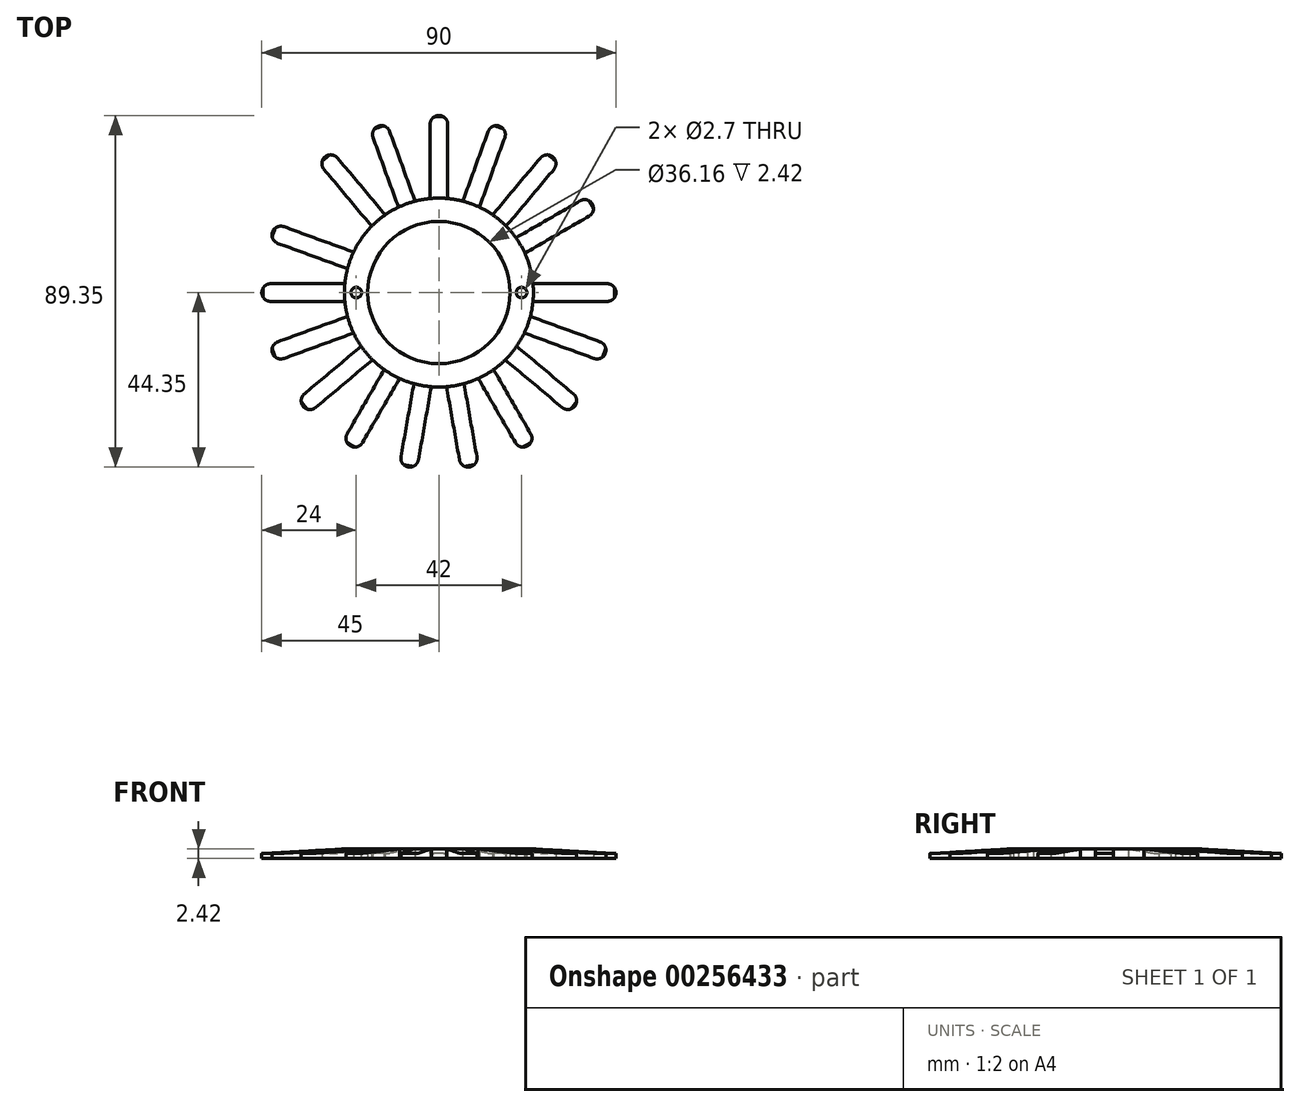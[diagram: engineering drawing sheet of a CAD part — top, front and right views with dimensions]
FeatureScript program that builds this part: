
annotation { "Feature Type Name" : "Feature", "Feature Type Description" : "" }
export const myFeature = defineFeature(function(context is Context, id is Id, definition is map)
    precondition{}
    {
        {
            var Q0;
            Q0=qCreatedBy(makeId("Top.planeOp"),FACE);
            var sketch = newSketch(context, id + "F0", { "sketchPlane" : qUnion([Q0])});
            skCircle(sketch, "E0", {"center": v(0, 0) * mm, "radius": 6.03 * mm});
            skCircle(sketch, "E1", {"center": v(0, 0) * mm, "radius": 8 * mm});
            skSolve(sketch);
        }
        {
            var Q0;
            Q0=makeQuery(id+"F0.imprint","IMPRINT",FACE,{"disambiguationData":[TD([[makeQuery(id+"F0.imprint","IMPRINT",EDGE,{"derivedFrom":sQuery(id+"F0.wireOp",EDGE,"E0")}),-1.0]])]});
            extrude(context, id + "F1", {"entities" : qUnion([Q0]), "depth" : 0.34 * mm});
        }
        {
            var Q0;
            Q0=qCreatedBy(makeId("Top.planeOp"),FACE);
            var sketch = newSketch(context, id + "F2", { "sketchPlane" : qUnion([Q0])});
            skCircle(sketch, "E2", {"center": v(0, 0) * mm, "radius": 8 * mm, "construction": true});
            skCircle(sketch, "E3", {"center": v(0, 0) * mm, "radius": 15 * mm, "construction": true});
            skArc(sketch, "E4", {"start": v(14.25, -0.75) * mm, "mid": v(15, 0) * mm, "end": v(14.25, 0.75) * mm});
            skLineSegment(sketch, "E5", {"start": v(14.25, -0.75) * mm, "end": v(7.96, -0.75) * mm});
            skLineSegment(sketch, "E6", {"start": v(14.25, 0.75) * mm, "end": v(7.96, 0.75) * mm});
            skLineSegment(sketch, "E7", {"start": v(7.96, 0.75) * mm, "end": v(7.96, -0.75) * mm});
            skSolve(sketch);
        }
        {
            var Q0;
            Q0=makeQuery(id+"F2.imprint","IMPRINT",FACE,{"disambiguationData":[TD([[makeQuery(id+"F2.imprint","IMPRINT",EDGE,{"derivedFrom":sQuery(id+"F2.wireOp",EDGE,"E4")}),1.0]])]});
            extrude(context, id + "F3", {"entities" : qUnion([Q0]), "depth" : 0.34 * mm});
        }
        {
            var Q0;
            Q0=qCreatedBy(makeId("Front.planeOp"),FACE);
            var sketch = newSketch(context, id + "F4", { "sketchPlane" : qUnion([Q0])});
            skLineSegment(sketch, "E8", {"start": v(0, 0) * mm, "end": v(0, 5.33) * mm, "construction": true});
            skSolve(sketch);
        }
        {
            var Q0;
            Q0=makeQuery(id+"F3.opExtrude","SWEPT_BODY",BODY,{"disambiguationData":[OSD([sQuery(id+"F2.wireOp",EDGE,"E4"),sQuery(id+"F2.wireOp",EDGE,"E5"),sQuery(id+"F2.wireOp",EDGE,"E6"),sQuery(id+"F2.wireOp",EDGE,"E7")])]});
            var Q1;
            Q1=sQuery(id+"F4.wireOp",EDGE,"E8");
            circularPattern(context, id + "F5", {"entities" : qUnion([Q0]), "axis" : qUnion([Q1]), "angle" : 20 * degree, "instanceCount" : 11, "oppositeDirection" : true, "computeTransformsWithoutBuiltin" : true});
        }
        {
            var Q0;
            Q0=qCreatedBy(makeId("Top.planeOp"),FACE);
            var sketch = newSketch(context, id + "F6", { "sketchPlane" : qUnion([Q0])});
            skCircle(sketch, "E9", {"center": v(0, 0) * mm, "radius": 15 * mm, "construction": true});
            skLineSegment(sketch, "E10", {"start": v(0, 0) * mm, "end": v(13, 7.5) * mm, "construction": true});
            skLineSegment(sketch, "E11", {"start": v(0, 0) * mm, "end": v(13.86, 0) * mm, "construction": true});
            skArc(sketch, "E12", {"start": v(12.72, 6.48) * mm, "mid": v(13, 7.5) * mm, "end": v(11.97, 7.77) * mm});
            skLineSegment(sketch, "E13", {"start": v(12.34, 7.13) * mm, "end": v(12.72, 6.48) * mm});
            skLineSegment(sketch, "E14", {"start": v(12.72, 6.48) * mm, "end": v(6.65, 2.98) * mm});
            skLineSegment(sketch, "E15", {"start": v(6.65, 2.98) * mm, "end": v(5.9, 4.27) * mm});
            skLineSegment(sketch, "E16", {"start": v(5.9, 4.27) * mm, "end": v(11.97, 7.77) * mm});
            skSolve(sketch);
        }
        {
            var Q0;
            Q0=makeQuery(id+"F6.imprint","IMPRINT",FACE,{"disambiguationData":[TD([[makeQuery(id+"F6.imprint","IMPRINT",EDGE,{"derivedFrom":sQuery(id+"F6.wireOp",EDGE,"E12")}),1.0]])]});
            extrude(context, id + "F7", {"entities" : qUnion([Q0]), "depth" : 0.34 * mm});
        }
        {
            var Q0;
            Q0=makeQuery(id+"F7.opExtrude","SWEPT_BODY",BODY,{"disambiguationData":[OSD([sQuery(id+"F6.wireOp",EDGE,"E12"),sQuery(id+"F6.wireOp",EDGE,"E14"),sQuery(id+"F6.wireOp",EDGE,"E15"),sQuery(id+"F6.wireOp",EDGE,"E16")])]});
            var Q1;
            Q1=sQuery(id+"F4.wireOp",EDGE,"E8");
            circularPattern(context, id + "F8", {"entities" : qUnion([Q0]), "axis" : qUnion([Q1]), "angle" : 20 * degree, "instanceCount" : 6, "computeTransformsWithoutBuiltin" : true});
        }
        {
            var Q0;
            Q0=makeQuery(id+"F1.opExtrude","SWEPT_BODY",BODY,{"disambiguationData":[OSD([sQuery(id+"F0.wireOp",EDGE,"E0"),sQuery(id+"F0.wireOp",EDGE,"E1")])]});
            var Q1;
            Q1=makeQuery(id+"F7.opExtrude","SWEPT_BODY",BODY,{"disambiguationData":[OSD([sQuery(id+"F6.wireOp",EDGE,"E12"),sQuery(id+"F6.wireOp",EDGE,"E14"),sQuery(id+"F6.wireOp",EDGE,"E15"),sQuery(id+"F6.wireOp",EDGE,"E16")])]});
            var Q2;
            Q2=makeQuery(id+"F8.opPattern","COPY",BODY,{"derivedFrom":makeQuery(id+"F7.opExtrude","SWEPT_BODY",BODY,{"disambiguationData":[OSD([sQuery(id+"F6.wireOp",EDGE,"E12"),sQuery(id+"F6.wireOp",EDGE,"E14"),sQuery(id+"F6.wireOp",EDGE,"E15"),sQuery(id+"F6.wireOp",EDGE,"E16")])]}),"instanceName":"1"});
            var Q3;
            Q3=makeQuery(id+"F8.opPattern","COPY",BODY,{"derivedFrom":makeQuery(id+"F7.opExtrude","SWEPT_BODY",BODY,{"disambiguationData":[OSD([sQuery(id+"F6.wireOp",EDGE,"E12"),sQuery(id+"F6.wireOp",EDGE,"E14"),sQuery(id+"F6.wireOp",EDGE,"E15"),sQuery(id+"F6.wireOp",EDGE,"E16")])]}),"instanceName":"2"});
            var Q4;
            Q4=makeQuery(id+"F8.opPattern","COPY",BODY,{"derivedFrom":makeQuery(id+"F7.opExtrude","SWEPT_BODY",BODY,{"disambiguationData":[OSD([sQuery(id+"F6.wireOp",EDGE,"E12"),sQuery(id+"F6.wireOp",EDGE,"E14"),sQuery(id+"F6.wireOp",EDGE,"E15"),sQuery(id+"F6.wireOp",EDGE,"E16")])]}),"instanceName":"3"});
            var Q5;
            Q5=makeQuery(id+"F8.opPattern","COPY",BODY,{"derivedFrom":makeQuery(id+"F7.opExtrude","SWEPT_BODY",BODY,{"disambiguationData":[OSD([sQuery(id+"F6.wireOp",EDGE,"E12"),sQuery(id+"F6.wireOp",EDGE,"E14"),sQuery(id+"F6.wireOp",EDGE,"E15"),sQuery(id+"F6.wireOp",EDGE,"E16")])]}),"instanceName":"4"});
            var Q6;
            Q6=makeQuery(id+"F8.opPattern","COPY",BODY,{"derivedFrom":makeQuery(id+"F7.opExtrude","SWEPT_BODY",BODY,{"disambiguationData":[OSD([sQuery(id+"F6.wireOp",EDGE,"E12"),sQuery(id+"F6.wireOp",EDGE,"E14"),sQuery(id+"F6.wireOp",EDGE,"E15"),sQuery(id+"F6.wireOp",EDGE,"E16")])]}),"instanceName":"5"});
            var Q7;
            Q7=makeQuery(id+"F5.opPattern","COPY",BODY,{"derivedFrom":makeQuery(id+"F3.opExtrude","SWEPT_BODY",BODY,{"disambiguationData":[OSD([sQuery(id+"F2.wireOp",EDGE,"E4"),sQuery(id+"F2.wireOp",EDGE,"E5"),sQuery(id+"F2.wireOp",EDGE,"E6"),sQuery(id+"F2.wireOp",EDGE,"E7")])]}),"instanceName":"10"});
            var Q8;
            Q8=makeQuery(id+"F5.opPattern","COPY",BODY,{"derivedFrom":makeQuery(id+"F3.opExtrude","SWEPT_BODY",BODY,{"disambiguationData":[OSD([sQuery(id+"F2.wireOp",EDGE,"E4"),sQuery(id+"F2.wireOp",EDGE,"E5"),sQuery(id+"F2.wireOp",EDGE,"E6"),sQuery(id+"F2.wireOp",EDGE,"E7")])]}),"instanceName":"9"});
            var Q9;
            Q9=makeQuery(id+"F5.opPattern","COPY",BODY,{"derivedFrom":makeQuery(id+"F3.opExtrude","SWEPT_BODY",BODY,{"disambiguationData":[OSD([sQuery(id+"F2.wireOp",EDGE,"E4"),sQuery(id+"F2.wireOp",EDGE,"E5"),sQuery(id+"F2.wireOp",EDGE,"E6"),sQuery(id+"F2.wireOp",EDGE,"E7")])]}),"instanceName":"8"});
            var Q10;
            Q10=makeQuery(id+"F5.opPattern","COPY",BODY,{"derivedFrom":makeQuery(id+"F3.opExtrude","SWEPT_BODY",BODY,{"disambiguationData":[OSD([sQuery(id+"F2.wireOp",EDGE,"E4"),sQuery(id+"F2.wireOp",EDGE,"E5"),sQuery(id+"F2.wireOp",EDGE,"E6"),sQuery(id+"F2.wireOp",EDGE,"E7")])]}),"instanceName":"7"});
            var Q11;
            Q11=makeQuery(id+"F5.opPattern","COPY",BODY,{"derivedFrom":makeQuery(id+"F3.opExtrude","SWEPT_BODY",BODY,{"disambiguationData":[OSD([sQuery(id+"F2.wireOp",EDGE,"E4"),sQuery(id+"F2.wireOp",EDGE,"E5"),sQuery(id+"F2.wireOp",EDGE,"E6"),sQuery(id+"F2.wireOp",EDGE,"E7")])]}),"instanceName":"6"});
            var Q12;
            Q12=makeQuery(id+"F5.opPattern","COPY",BODY,{"derivedFrom":makeQuery(id+"F3.opExtrude","SWEPT_BODY",BODY,{"disambiguationData":[OSD([sQuery(id+"F2.wireOp",EDGE,"E4"),sQuery(id+"F2.wireOp",EDGE,"E5"),sQuery(id+"F2.wireOp",EDGE,"E6"),sQuery(id+"F2.wireOp",EDGE,"E7")])]}),"instanceName":"4"});
            var Q13;
            Q13=makeQuery(id+"F5.opPattern","COPY",BODY,{"derivedFrom":makeQuery(id+"F3.opExtrude","SWEPT_BODY",BODY,{"disambiguationData":[OSD([sQuery(id+"F2.wireOp",EDGE,"E4"),sQuery(id+"F2.wireOp",EDGE,"E5"),sQuery(id+"F2.wireOp",EDGE,"E6"),sQuery(id+"F2.wireOp",EDGE,"E7")])]}),"instanceName":"5"});
            var Q14;
            Q14=makeQuery(id+"F5.opPattern","COPY",BODY,{"derivedFrom":makeQuery(id+"F3.opExtrude","SWEPT_BODY",BODY,{"disambiguationData":[OSD([sQuery(id+"F2.wireOp",EDGE,"E4"),sQuery(id+"F2.wireOp",EDGE,"E5"),sQuery(id+"F2.wireOp",EDGE,"E6"),sQuery(id+"F2.wireOp",EDGE,"E7")])]}),"instanceName":"3"});
            var Q15;
            Q15=makeQuery(id+"F5.opPattern","COPY",BODY,{"derivedFrom":makeQuery(id+"F3.opExtrude","SWEPT_BODY",BODY,{"disambiguationData":[OSD([sQuery(id+"F2.wireOp",EDGE,"E4"),sQuery(id+"F2.wireOp",EDGE,"E5"),sQuery(id+"F2.wireOp",EDGE,"E6"),sQuery(id+"F2.wireOp",EDGE,"E7")])]}),"instanceName":"2"});
            var Q16;
            Q16=makeQuery(id+"F5.opPattern","COPY",BODY,{"derivedFrom":makeQuery(id+"F3.opExtrude","SWEPT_BODY",BODY,{"disambiguationData":[OSD([sQuery(id+"F2.wireOp",EDGE,"E4"),sQuery(id+"F2.wireOp",EDGE,"E5"),sQuery(id+"F2.wireOp",EDGE,"E6"),sQuery(id+"F2.wireOp",EDGE,"E7")])]}),"instanceName":"1"});
            var Q17;
            Q17=makeQuery(id+"F3.opExtrude","SWEPT_BODY",BODY,{"disambiguationData":[OSD([sQuery(id+"F2.wireOp",EDGE,"E4"),sQuery(id+"F2.wireOp",EDGE,"E5"),sQuery(id+"F2.wireOp",EDGE,"E6"),sQuery(id+"F2.wireOp",EDGE,"E7")])]});
            booleanBodies(context, id + "F9", {"operationType" : BooleanOperationType.UNION, "tools" : qUnion([Q0, Q1, Q2, Q3, Q4, Q5, Q6, Q7, Q8, Q9, Q10, Q11, Q12, Q13, Q14, Q15, Q16, Q17])});
        }
        {
            var Q0;
            {var subQ0=makeQuery(id+"F3.opExtrude","CAP_FACE",FACE,{"disambiguationData":[OSD([sQuery(id+"F2.wireOp",EDGE,"E4"),sQuery(id+"F2.wireOp",EDGE,"E5"),sQuery(id+"F2.wireOp",EDGE,"E6"),sQuery(id+"F2.wireOp",EDGE,"E7")])],"isStart":false});var subQ1=makeQuery(id+"F7.opExtrude","CAP_FACE",FACE,{"disambiguationData":[OSD([sQuery(id+"F6.wireOp",EDGE,"E12"),sQuery(id+"F6.wireOp",EDGE,"E14"),sQuery(id+"F6.wireOp",EDGE,"E15"),sQuery(id+"F6.wireOp",EDGE,"E16")])],"isStart":false});Q0=makeQuery(id+"F9.opBoolean","MERGE",FACE,{"derivedFrom":[makeQuery(id+"F1.opExtrude","CAP_FACE",FACE,{"disambiguationData":[OSD([sQuery(id+"F0.wireOp",EDGE,"E0"),sQuery(id+"F0.wireOp",EDGE,"E1")])],"isStart":false}),subQ0,makeQuery(id+"F5.opPattern","COPY",FACE,{"derivedFrom":subQ0,"instanceName":"1"}),makeQuery(id+"F5.opPattern","COPY",FACE,{"derivedFrom":subQ0,"instanceName":"2"}),makeQuery(id+"F5.opPattern","COPY",FACE,{"derivedFrom":subQ0,"instanceName":"3"}),makeQuery(id+"F5.opPattern","COPY",FACE,{"derivedFrom":subQ0,"instanceName":"4"}),makeQuery(id+"F5.opPattern","COPY",FACE,{"derivedFrom":subQ0,"instanceName":"5"}),makeQuery(id+"F5.opPattern","COPY",FACE,{"derivedFrom":subQ0,"instanceName":"6"}),makeQuery(id+"F5.opPattern","COPY",FACE,{"derivedFrom":subQ0,"instanceName":"7"}),makeQuery(id+"F5.opPattern","COPY",FACE,{"derivedFrom":subQ0,"instanceName":"8"}),makeQuery(id+"F5.opPattern","COPY",FACE,{"derivedFrom":subQ0,"instanceName":"9"}),makeQuery(id+"F5.opPattern","COPY",FACE,{"derivedFrom":subQ0,"instanceName":"10"}),subQ1,makeQuery(id+"F8.opPattern","COPY",FACE,{"derivedFrom":subQ1,"instanceName":"1"}),makeQuery(id+"F8.opPattern","COPY",FACE,{"derivedFrom":subQ1,"instanceName":"2"}),makeQuery(id+"F8.opPattern","COPY",FACE,{"derivedFrom":subQ1,"instanceName":"3"}),makeQuery(id+"F8.opPattern","COPY",FACE,{"derivedFrom":subQ1,"instanceName":"4"}),makeQuery(id+"F8.opPattern","COPY",FACE,{"derivedFrom":subQ1,"instanceName":"5"})]});}
            var sketch = newSketch(context, id + "F10", { "sketchPlane" : qUnion([Q0])});
            skCircle(sketch, "E17", {"center": v(0, 0) * mm, "radius": 7 * mm, "construction": true});
            skCircle(sketch, "E18", {"center": v(7, 0) * mm, "radius": 0.45 * mm});
            skCircle(sketch, "E19", {"center": v(-7, 0) * mm, "radius": 0.45 * mm});
            skSolve(sketch);
        }
        {
            var Q0;
            {Q0=qUnion([makeQuery(id+"F10.imprint","IMPRINT",FACE,{"disambiguationData":[TD([[makeQuery(id+"F10.imprint","IMPRINT",EDGE,{"derivedFrom":sQuery(id+"F10.wireOp",EDGE,"E18")}),1.0]])]}),makeQuery(id+"F10.imprint","IMPRINT",FACE,{"disambiguationData":[TD([[makeQuery(id+"F10.imprint","IMPRINT",EDGE,{"derivedFrom":sQuery(id+"F10.wireOp",EDGE,"E19")}),1.0]])]})]);}
            var Q2;
            {var subQ0=makeQuery(id+"F7.opExtrude","CAP_FACE",FACE,{"disambiguationData":[OSD([sQuery(id+"F6.wireOp",EDGE,"E12"),sQuery(id+"F6.wireOp",EDGE,"E14"),sQuery(id+"F6.wireOp",EDGE,"E15"),sQuery(id+"F6.wireOp",EDGE,"E16")])],"isStart":true});var subQ1=makeQuery(id+"F3.opExtrude","CAP_FACE",FACE,{"disambiguationData":[OSD([sQuery(id+"F2.wireOp",EDGE,"E4"),sQuery(id+"F2.wireOp",EDGE,"E5"),sQuery(id+"F2.wireOp",EDGE,"E6"),sQuery(id+"F2.wireOp",EDGE,"E7")])],"isStart":true});Q2=makeQuery(id+"F9.opBoolean","MERGE",FACE,{"derivedFrom":[makeQuery(id+"F1.opExtrude","CAP_FACE",FACE,{"disambiguationData":[OSD([sQuery(id+"F0.wireOp",EDGE,"E0"),sQuery(id+"F0.wireOp",EDGE,"E1")])],"isStart":true}),subQ1,makeQuery(id+"F5.opPattern","COPY",FACE,{"derivedFrom":subQ1,"instanceName":"1"}),makeQuery(id+"F5.opPattern","COPY",FACE,{"derivedFrom":subQ1,"instanceName":"2"}),makeQuery(id+"F5.opPattern","COPY",FACE,{"derivedFrom":subQ1,"instanceName":"3"}),makeQuery(id+"F5.opPattern","COPY",FACE,{"derivedFrom":subQ1,"instanceName":"4"}),makeQuery(id+"F5.opPattern","COPY",FACE,{"derivedFrom":subQ1,"instanceName":"5"}),makeQuery(id+"F5.opPattern","COPY",FACE,{"derivedFrom":subQ1,"instanceName":"6"}),makeQuery(id+"F5.opPattern","COPY",FACE,{"derivedFrom":subQ1,"instanceName":"7"}),makeQuery(id+"F5.opPattern","COPY",FACE,{"derivedFrom":subQ1,"instanceName":"8"}),makeQuery(id+"F5.opPattern","COPY",FACE,{"derivedFrom":subQ1,"instanceName":"9"}),makeQuery(id+"F5.opPattern","COPY",FACE,{"derivedFrom":subQ1,"instanceName":"10"}),subQ0,makeQuery(id+"F8.opPattern","COPY",FACE,{"derivedFrom":subQ0,"instanceName":"1"}),makeQuery(id+"F8.opPattern","COPY",FACE,{"derivedFrom":subQ0,"instanceName":"2"}),makeQuery(id+"F8.opPattern","COPY",FACE,{"derivedFrom":subQ0,"instanceName":"3"}),makeQuery(id+"F8.opPattern","COPY",FACE,{"derivedFrom":subQ0,"instanceName":"4"}),makeQuery(id+"F8.opPattern","COPY",FACE,{"derivedFrom":subQ0,"instanceName":"5"})]});}
            extrude(context, id + "F11", {"entities" : qUnion([Q0]), "operationType" : NewBodyOperationType.REMOVE, "endBound" : BoundingType.UP_TO_SURFACE, "oppositeDirection" : true, "depth" : 0.14 * mm, "endBoundEntityFace" : qUnion([Q2])});
        }
        {
            var Q0;
            Q0=makeQuery(id+"F1.opExtrude","SWEPT_BODY",BODY,{"disambiguationData":[OSD([sQuery(id+"F0.wireOp",EDGE,"E0"),sQuery(id+"F0.wireOp",EDGE,"E1")])]});
            var Q1;
            Q1=sQuery(id+"F4.wireOp",VERTEX,"E8.start");
            transform(context, id + "F12", {"entities" : qUnion([Q0]), "transformType" : TransformType.SCALE_UNIFORMLY, "scale" : 3, "makeCopy" : false, "scalePoint" : qUnion([Q1])});
        }
        {
            var Q0;
            Q0=qCreatedBy(makeId("Front.planeOp"),FACE);
            var sketch = newSketch(context, id + "F15", { "sketchPlane" : qUnion([Q0])});
            skLineSegment(sketch, "E20", {"start": v(18, 0) * mm, "end": v(45, 0) * mm});
            skLineSegment(sketch, "E21", {"start": v(45, 1) * mm, "end": v(24, 2.22) * mm});
            skLineSegment(sketch, "E22", {"start": v(18, 2.22) * mm, "end": v(18, 0) * mm});
            skLineSegment(sketch, "E23", {"start": v(45, 0) * mm, "end": v(45, 1) * mm});
            skLineSegment(sketch, "E24", {"start": v(24, 2.22) * mm, "end": v(18, 2.22) * mm});
            skSolve(sketch);
        }
        {
            var Q0;
            Q0=qSketchRegion(id+"F15",true);
            var Q1;
            Q1=sQuery(id+"F4.wireOp",EDGE,"E8");
            revolve(context, id + "F13", {"entities" : qUnion([Q0]), "axis" : qUnion([Q1]), "revolveType" : RevolveType.FULL});
        }
        {
            var Q0;
            {var subQ0=makeQuery(id+"F7.opExtrude","CAP_FACE",FACE,{"disambiguationData":[OSD([sQuery(id+"F6.wireOp",EDGE,"E12"),sQuery(id+"F6.wireOp",EDGE,"E14"),sQuery(id+"F6.wireOp",EDGE,"E15"),sQuery(id+"F6.wireOp",EDGE,"E16")])],"isStart":true});var subQ1=makeQuery(id+"F3.opExtrude","CAP_FACE",FACE,{"disambiguationData":[OSD([sQuery(id+"F2.wireOp",EDGE,"E4"),sQuery(id+"F2.wireOp",EDGE,"E5"),sQuery(id+"F2.wireOp",EDGE,"E6"),sQuery(id+"F2.wireOp",EDGE,"E7")])],"isStart":true});Q0=makeQuery(id+"F9.opBoolean","MERGE",FACE,{"derivedFrom":[makeQuery(id+"F1.opExtrude","CAP_FACE",FACE,{"disambiguationData":[OSD([sQuery(id+"F0.wireOp",EDGE,"E0"),sQuery(id+"F0.wireOp",EDGE,"E1")])],"isStart":true}),subQ1,makeQuery(id+"F5.opPattern","COPY",FACE,{"derivedFrom":subQ1,"instanceName":"1"}),makeQuery(id+"F5.opPattern","COPY",FACE,{"derivedFrom":subQ1,"instanceName":"2"}),makeQuery(id+"F5.opPattern","COPY",FACE,{"derivedFrom":subQ1,"instanceName":"3"}),makeQuery(id+"F5.opPattern","COPY",FACE,{"derivedFrom":subQ1,"instanceName":"4"}),makeQuery(id+"F5.opPattern","COPY",FACE,{"derivedFrom":subQ1,"instanceName":"5"}),makeQuery(id+"F5.opPattern","COPY",FACE,{"derivedFrom":subQ1,"instanceName":"6"}),makeQuery(id+"F5.opPattern","COPY",FACE,{"derivedFrom":subQ1,"instanceName":"7"}),makeQuery(id+"F5.opPattern","COPY",FACE,{"derivedFrom":subQ1,"instanceName":"8"}),makeQuery(id+"F5.opPattern","COPY",FACE,{"derivedFrom":subQ1,"instanceName":"9"}),makeQuery(id+"F5.opPattern","COPY",FACE,{"derivedFrom":subQ1,"instanceName":"10"}),subQ0,makeQuery(id+"F8.opPattern","COPY",FACE,{"derivedFrom":subQ0,"instanceName":"1"}),makeQuery(id+"F8.opPattern","COPY",FACE,{"derivedFrom":subQ0,"instanceName":"2"}),makeQuery(id+"F8.opPattern","COPY",FACE,{"derivedFrom":subQ0,"instanceName":"3"}),makeQuery(id+"F8.opPattern","COPY",FACE,{"derivedFrom":subQ0,"instanceName":"4"}),makeQuery(id+"F8.opPattern","COPY",FACE,{"derivedFrom":subQ0,"instanceName":"5"})]});}
            extrude(context, id + "F16", {"entities" : qUnion([Q0]), "operationType" : NewBodyOperationType.INTERSECT, "oppositeDirection" : true, "depth" : 2.22 * mm});
        }
        {
            var Q0;
            {var subQ0=makeQuery(id+"F7.opExtrude","CAP_FACE",FACE,{"disambiguationData":[OSD([sQuery(id+"F6.wireOp",EDGE,"E12"),sQuery(id+"F6.wireOp",EDGE,"E14"),sQuery(id+"F6.wireOp",EDGE,"E15"),sQuery(id+"F6.wireOp",EDGE,"E16")])],"isStart":true});var subQ1=makeQuery(id+"F3.opExtrude","CAP_FACE",FACE,{"disambiguationData":[OSD([sQuery(id+"F2.wireOp",EDGE,"E4"),sQuery(id+"F2.wireOp",EDGE,"E5"),sQuery(id+"F2.wireOp",EDGE,"E6"),sQuery(id+"F2.wireOp",EDGE,"E7")])],"isStart":true});Q0=makeQuery(id+"F9.opBoolean","MERGE",FACE,{"derivedFrom":[makeQuery(id+"F1.opExtrude","CAP_FACE",FACE,{"disambiguationData":[OSD([sQuery(id+"F0.wireOp",EDGE,"E0"),sQuery(id+"F0.wireOp",EDGE,"E1")])],"isStart":true}),subQ1,makeQuery(id+"F5.opPattern","COPY",FACE,{"derivedFrom":subQ1,"instanceName":"1"}),makeQuery(id+"F5.opPattern","COPY",FACE,{"derivedFrom":subQ1,"instanceName":"2"}),makeQuery(id+"F5.opPattern","COPY",FACE,{"derivedFrom":subQ1,"instanceName":"3"}),makeQuery(id+"F5.opPattern","COPY",FACE,{"derivedFrom":subQ1,"instanceName":"4"}),makeQuery(id+"F5.opPattern","COPY",FACE,{"derivedFrom":subQ1,"instanceName":"5"}),makeQuery(id+"F5.opPattern","COPY",FACE,{"derivedFrom":subQ1,"instanceName":"6"}),makeQuery(id+"F5.opPattern","COPY",FACE,{"derivedFrom":subQ1,"instanceName":"7"}),makeQuery(id+"F5.opPattern","COPY",FACE,{"derivedFrom":subQ1,"instanceName":"8"}),makeQuery(id+"F5.opPattern","COPY",FACE,{"derivedFrom":subQ1,"instanceName":"9"}),makeQuery(id+"F5.opPattern","COPY",FACE,{"derivedFrom":subQ1,"instanceName":"10"}),subQ0,makeQuery(id+"F8.opPattern","COPY",FACE,{"derivedFrom":subQ0,"instanceName":"1"}),makeQuery(id+"F8.opPattern","COPY",FACE,{"derivedFrom":subQ0,"instanceName":"2"}),makeQuery(id+"F8.opPattern","COPY",FACE,{"derivedFrom":subQ0,"instanceName":"3"}),makeQuery(id+"F8.opPattern","COPY",FACE,{"derivedFrom":subQ0,"instanceName":"4"}),makeQuery(id+"F8.opPattern","COPY",FACE,{"derivedFrom":subQ0,"instanceName":"5"})]});}
            extrude(context, id + "F14", {"entities" : qUnion([Q0]), "operationType" : NewBodyOperationType.ADD, "depth" : 0.2 * mm});
        }
    });
